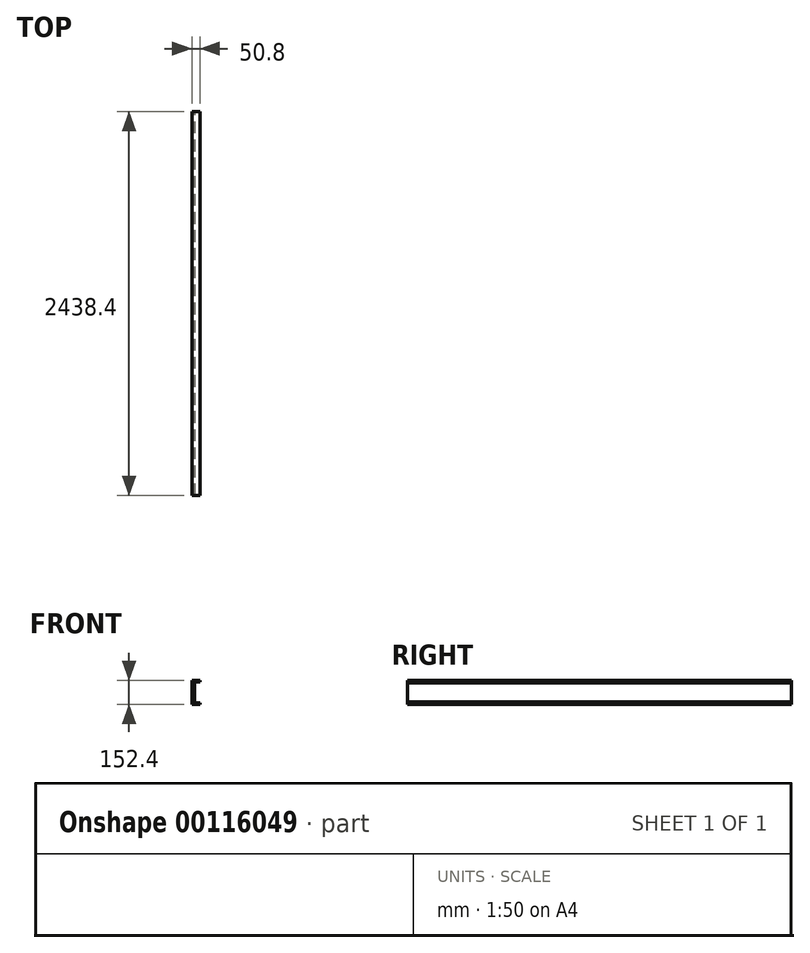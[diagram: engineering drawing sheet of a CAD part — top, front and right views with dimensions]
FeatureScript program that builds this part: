
annotation { "Feature Type Name" : "Feature", "Feature Type Description" : "" }
export const myFeature = defineFeature(function(context is Context, id is Id, definition is map)
    precondition{}
    {
        {
            var Q0;
            Q0=qCreatedBy(makeId("Front.planeOp"),FACE);
            var sketch = newSketch(context, id + "F0", { "sketchPlane" : qUnion([Q0])});
            skLineSegment(sketch, "E0", {"start": v(0, 0) * mm, "end": v(0, 152.4) * mm});
            skLineSegment(sketch, "E1", {"start": v(0, 152.4) * mm, "end": v(50.8, 152.4) * mm});
            skLineSegment(sketch, "E2", {"start": v(50.8, 152.4) * mm, "end": v(50.8, 142.88) * mm});
            skArc(sketch, "E3", {"start": v(19.71, 140.97) * mm, "mid": v(16.73, 139.6) * mm, "end": v(15.68, 136.48) * mm});
            skLineSegment(sketch, "E4", {"start": v(19.71, 140.97) * mm, "end": v(50.8, 142.88) * mm});
            skLineSegment(sketch, "E5", {"start": v(15.68, 136.48) * mm, "end": v(15.68, 76.2) * mm});
            skLineSegment(sketch, "E6.MirrorCS", {"start": v(0, 152.4) * mm, "end": v(0, 0) * mm});
            skLineSegment(sketch, "E7.MirrorCS", {"start": v(0, 0) * mm, "end": v(50.8, 0) * mm});
            skLineSegment(sketch, "E8.MirrorCS", {"start": v(50.8, 0) * mm, "end": v(50.8, 9.53) * mm});
            skLineSegment(sketch, "E9.MirrorCS", {"start": v(19.71, 11.43) * mm, "end": v(50.8, 9.53) * mm});
            skLineSegment(sketch, "E10.MirrorCS", {"start": v(15.68, 15.92) * mm, "end": v(15.68, 76.2) * mm});
            skArc(sketch, "E11.MirrorCS", {"start": v(19.71, 11.43) * mm, "mid": v(16.73, 12.8) * mm, "end": v(15.68, 15.92) * mm});
            skSolve(sketch);
        }
        {
            var Q0;
            Q0=makeQuery(id+"F0.imprint","IMPRINT",FACE,{"disambiguationData":[TD([[makeQuery(id+"F0.imprint","IMPRINT",EDGE,{"derivedFrom":sQuery(id+"F0.wireOp",EDGE,"E1")}),-1.0]])]});
            extrude(context, id + "F1", {"entities" : qUnion([Q0]), "depth" : 2438.4 * mm});
        }
    });
